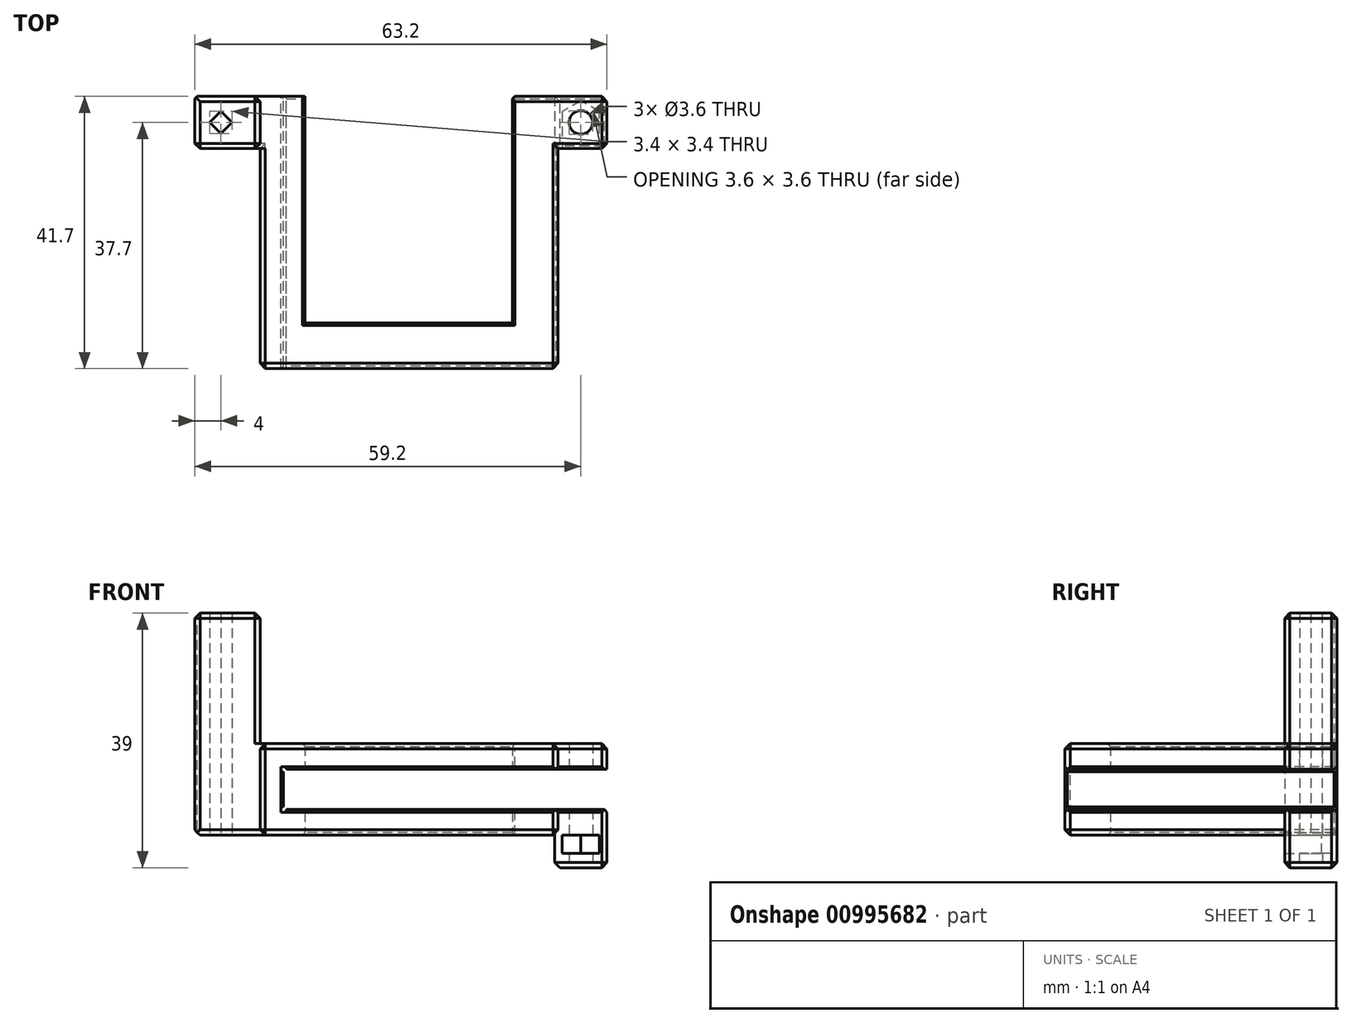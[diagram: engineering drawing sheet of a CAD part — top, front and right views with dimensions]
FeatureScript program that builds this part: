
annotation { "Feature Type Name" : "Feature", "Feature Type Description" : "" }
export const myFeature = defineFeature(function(context is Context, id is Id, definition is map)
    precondition{}
    {
        {
            var Q0;
            Q0=qCreatedBy(makeId("Top.planeOp"),FACE);
            var sketch = newSketch(context, id + "F0", { "sketchPlane" : qUnion([Q0])});
            skLineSegment(sketch, "E0.bottom", {"start": v(0, 0) * mm, "end": v(31.6, 0) * mm, "construction": true});
            skLineSegment(sketch, "E0.top", {"start": v(0, -31.6) * mm, "end": v(31.6, -31.6) * mm, "construction": true});
            skLineSegment(sketch, "E0.left", {"start": v(0, 0) * mm, "end": v(0, -31.6) * mm, "construction": true});
            skLineSegment(sketch, "E0.right", {"start": v(31.6, 0) * mm, "end": v(31.6, -31.6) * mm, "construction": true});
            skLineSegment(sketch, "E1.bottom", {"start": v(-3, 2) * mm, "end": v(57, 2) * mm, "construction": true});
            skLineSegment(sketch, "E1.top", {"start": v(-3, -48) * mm, "end": v(57, -48) * mm, "construction": true});
            skLineSegment(sketch, "E1.left", {"start": v(-3, 2) * mm, "end": v(-3, -48) * mm, "construction": true});
            skLineSegment(sketch, "E1.right", {"start": v(57, 2) * mm, "end": v(57, -48) * mm, "construction": true});
            skCircle(sketch, "E2", {"center": v(42.2, -1) * mm, "radius": 1.8 * mm});
            skLineSegment(sketch, "E3.bottom", {"start": v(-0.1, 2) * mm, "end": v(-7, 2) * mm});
            skLineSegment(sketch, "E3.top", {"start": v(-0.1, -38.7) * mm, "end": v(-7, -38.7) * mm});
            skLineSegment(sketch, "E3.left", {"start": v(-0.1, 2) * mm, "end": v(-0.1, -38.7) * mm});
            skLineSegment(sketch, "E3.right", {"start": v(-7, 2) * mm, "end": v(-7, -38.7) * mm});
            skLineSegment(sketch, "E4.bottom", {"start": v(-0.1, -38.7) * mm, "end": v(31.7, -38.7) * mm});
            skLineSegment(sketch, "E4.top", {"start": v(-0.1, -31.7) * mm, "end": v(31.7, -31.7) * mm});
            skLineSegment(sketch, "E4.left", {"start": v(-0.1, -38.7) * mm, "end": v(-0.1, -31.7) * mm});
            skLineSegment(sketch, "E4.right", {"start": v(31.7, -38.7) * mm, "end": v(31.7, -31.7) * mm});
            skLineSegment(sketch, "E5.bottom", {"start": v(31.7, -38.7) * mm, "end": v(38.7, -38.7) * mm});
            skLineSegment(sketch, "E5.top", {"start": v(31.7, 2) * mm, "end": v(38.7, 2) * mm});
            skLineSegment(sketch, "E5.left", {"start": v(31.7, -38.7) * mm, "end": v(31.7, 2) * mm});
            skLineSegment(sketch, "E5.right", {"start": v(38.7, -38.7) * mm, "end": v(38.7, 2) * mm});
            skLineSegment(sketch, "E6.bottom", {"start": v(38.7, 2) * mm, "end": v(46.2, 2) * mm});
            skLineSegment(sketch, "E6.top", {"start": v(38.7, -5) * mm, "end": v(46.2, -5) * mm});
            skLineSegment(sketch, "E6.left", {"start": v(38.7, 2) * mm, "end": v(38.7, -5) * mm});
            skLineSegment(sketch, "E6.right", {"start": v(46.2, 2) * mm, "end": v(46.2, -5) * mm});
            skCircle(sketch, "E7", {"center": v(42.2, -1) * mm, "radius": 4 * mm, "construction": true});
            skLineSegment(sketch, "E8.bottom", {"start": v(31.7, 2) * mm, "end": v(46.2, 2) * mm});
            skLineSegment(sketch, "E8.top", {"start": v(31.7, 3) * mm, "end": v(46.2, 3) * mm});
            skLineSegment(sketch, "E8.left", {"start": v(31.7, 2) * mm, "end": v(31.7, 3) * mm});
            skLineSegment(sketch, "E8.right", {"start": v(46.2, 2) * mm, "end": v(46.2, 3) * mm});
            skLineSegment(sketch, "E9.bottom", {"start": v(-7, 2) * mm, "end": v(-0.1, 2) * mm});
            skLineSegment(sketch, "E9.top", {"start": v(-7, 3) * mm, "end": v(-0.1, 3) * mm});
            skLineSegment(sketch, "E9.left", {"start": v(-7, 2) * mm, "end": v(-7, 3) * mm});
            skLineSegment(sketch, "E9.right", {"start": v(-0.1, 2) * mm, "end": v(-0.1, 3) * mm});
            skLineSegment(sketch, "E10", {"start": v(57, 2) * mm, "end": v(57, 8) * mm, "construction": true});
            skLineSegment(sketch, "E11.bottom", {"start": v(-7, 8) * mm, "end": v(57, 8) * mm, "construction": true});
            skLineSegment(sketch, "E11.top", {"start": v(-7, 5) * mm, "end": v(57, 5) * mm, "construction": true});
            skLineSegment(sketch, "E11.left", {"start": v(-7, 8) * mm, "end": v(-7, 5) * mm, "construction": true});
            skLineSegment(sketch, "E11.right", {"start": v(57, 8) * mm, "end": v(57, 5) * mm, "construction": true});
            skLineSegment(sketch, "E12", {"start": v(-7, 8) * mm, "end": v(-47, 8) * mm, "construction": true});
            skCircle(sketch, "E13", {"center": v(-13, -1) * mm, "radius": 4 * mm, "construction": true});
            skLineSegment(sketch, "E14.bottom", {"start": v(-0.1, 3) * mm, "end": v(-17, 3) * mm});
            skLineSegment(sketch, "E14.top", {"start": v(-0.1, -5) * mm, "end": v(-17, -5) * mm});
            skLineSegment(sketch, "E14.left", {"start": v(-0.1, 3) * mm, "end": v(-0.1, -5) * mm});
            skLineSegment(sketch, "E14.right", {"start": v(-17, 3) * mm, "end": v(-17, -5) * mm});
            skCircle(sketch, "E15", {"center": v(-13, -1) * mm, "radius": 1.7 * mm, "construction": true});
            skLineSegment(sketch, "E16.0", {"start": v(-11.3, -1) * mm, "end": v(-13, -2.7) * mm});
            skLineSegment(sketch, "E16.1", {"start": v(-13, -2.7) * mm, "end": v(-14.7, -1) * mm});
            skLineSegment(sketch, "E16.2", {"start": v(-14.7, -1) * mm, "end": v(-13, 0.7) * mm});
            skLineSegment(sketch, "E16.3", {"start": v(-13, 0.7) * mm, "end": v(-11.3, -1) * mm});
            skSolve(sketch);
        }
        {
            var Q0;
            {var subQ5=sQuery(id+"F0.wireOp",EDGE,"E9.left");Q0=makeQuery(id+"F0.imprint","IMPRINT",FACE,{"disambiguationData":[TD([[makeQuery(id+"F0.imprint","IMPRINT",EDGE,{"derivedFrom":subQ5}),1.0]])]});}
            extrude(context, id + "F1", {"entities" : qUnion([Q0]), "depth" : 27 * mm, "offsetDistance" : 25 * mm});
        }
        {
            var Q0;
            {var subQ5=sQuery(id+"F0.wireOp",EDGE,"E9.left");Q0=makeQuery(id+"F0.imprint","IMPRINT",FACE,{"disambiguationData":[TD([[makeQuery(id+"F0.imprint","IMPRINT",EDGE,{"derivedFrom":subQ5}),1.0]])]});}
            extrude(context, id + "F2", {"entities" : qUnion([Q0]), "operationType" : NewBodyOperationType.ADD, "oppositeDirection" : true, "depth" : 6 * mm, "offsetDistance" : 25 * mm});
        }
        {
            var Q0;
            Q0 = qSketchRegion(id + "F0", true);
            extrude(context, id + "F3", {"entities" : qUnion([Q0]), "operationType" : NewBodyOperationType.ADD, "endBound" : BoundingType.SYMMETRIC, "depth" : 14 * mm, "offsetDistance" : 25 * mm});
        }
        {
            var Q0;
            Q0=makeQuery(id+"F3.opExtrude","SWEPT_FACE",FACE,{"disambiguationData":[OSD([sQuery(id+"F0.wireOp",EDGE,"E8.top")])]});
            var sketch = newSketch(context, id + "F4", { "sketchPlane" : qUnion([Q0])});
            skLineSegment(sketch, "E17.bottom", {"start": v(-46.2, 3.1) * mm, "end": v(3.4, 3.1) * mm});
            skLineSegment(sketch, "E17.top", {"start": v(-46.2, -3.1) * mm, "end": v(3.4, -3.1) * mm});
            skLineSegment(sketch, "E17.left", {"start": v(-46.2, 3.1) * mm, "end": v(-46.2, -3.1) * mm});
            skLineSegment(sketch, "E17.right", {"start": v(3.4, 3.1) * mm, "end": v(3.4, -3.1) * mm});
            skPoint(sketch, "E17.middle", {"position": v(-21.4, 0) * mm});
            skPoint(sketch, "E18.0", {"position": v(3, 0) * mm});
            skLineSegment(sketch, "E19.bottom", {"start": v(3, 3.5) * mm, "end": v(3.8, 3.5) * mm});
            skLineSegment(sketch, "E19.top", {"start": v(3, 2.7) * mm, "end": v(3.8, 2.7) * mm});
            skLineSegment(sketch, "E19.left", {"start": v(3, 3.5) * mm, "end": v(3, 2.7) * mm});
            skLineSegment(sketch, "E19.right", {"start": v(3.8, 3.5) * mm, "end": v(3.8, 2.7) * mm});
            skPoint(sketch, "E19.middle", {"position": v(3.4, 3.1) * mm});
            skLineSegment(sketch, "E20.bottom", {"start": v(3, -2.7) * mm, "end": v(3.8, -2.7) * mm});
            skLineSegment(sketch, "E20.top", {"start": v(3, -3.5) * mm, "end": v(3.8, -3.5) * mm});
            skLineSegment(sketch, "E20.left", {"start": v(3, -2.7) * mm, "end": v(3, -3.5) * mm});
            skLineSegment(sketch, "E20.right", {"start": v(3.8, -2.7) * mm, "end": v(3.8, -3.5) * mm});
            skPoint(sketch, "E20.middle", {"position": v(3.4, -3.1) * mm});
            skSolve(sketch);
        }
        {
            var Q0;
            Q0 = qSketchRegion(id + "F4", true);
            var Q1;
            Q1=makeQuery(id+"F3.opExtrude","SWEPT_FACE",FACE,{"disambiguationData":[OSD([sQuery(id+"F0.wireOp",EDGE,"E3.top"),sQuery(id+"F0.wireOp",EDGE,"E4.bottom"),sQuery(id+"F0.wireOp",EDGE,"E5.bottom")])]});
            extrude(context, id + "F5", {"entities" : qUnion([Q0]), "operationType" : NewBodyOperationType.REMOVE, "endBound" : BoundingType.SYMMETRIC, "oppositeDirection" : true, "depth" : 100 * mm, "endBoundEntityFace" : qUnion([Q1]), "offsetDistance" : 25 * mm});
        }
        {
            var Q0;
            Q0=makeQuery(id+"F3.opExtrude","CAP_FACE",FACE,{"disambiguationData":[OSD([sQuery(id+"F0.wireOp",EDGE,"E2"),sQuery(id+"F0.wireOp",EDGE,"E3.top"),sQuery(id+"F0.wireOp",EDGE,"E3.left"),sQuery(id+"F0.wireOp",EDGE,"E3.right"),sQuery(id+"F0.wireOp",EDGE,"E4.bottom"),sQuery(id+"F0.wireOp",EDGE,"E4.top"),sQuery(id+"F0.wireOp",EDGE,"E5.bottom"),sQuery(id+"F0.wireOp",EDGE,"E5.left"),sQuery(id+"F0.wireOp",EDGE,"E5.right"),sQuery(id+"F0.wireOp",EDGE,"E6.top"),sQuery(id+"F0.wireOp",EDGE,"E6.right"),sQuery(id+"F0.wireOp",EDGE,"E8.top"),sQuery(id+"F0.wireOp",EDGE,"E8.left"),sQuery(id+"F0.wireOp",EDGE,"E8.right"),sQuery(id+"F0.wireOp",EDGE,"E14.bottom"),sQuery(id+"F0.wireOp",EDGE,"E14.top"),sQuery(id+"F0.wireOp",EDGE,"E14.left"),sQuery(id+"F0.wireOp",EDGE,"E14.right"),sQuery(id+"F0.wireOp",EDGE,"E16.0"),sQuery(id+"F0.wireOp",EDGE,"E16.1"),sQuery(id+"F0.wireOp",EDGE,"E16.2"),sQuery(id+"F0.wireOp",EDGE,"E16.3")])],"isStart":true});
            var sketch = newSketch(context, id + "F6", { "sketchPlane" : qUnion([Q0])});
            skLineSegment(sketch, "E21.bottom", {"start": v(46.2, -3) * mm, "end": v(38.2, -3) * mm});
            skLineSegment(sketch, "E21.top", {"start": v(46.2, 5) * mm, "end": v(38.2, 5) * mm});
            skLineSegment(sketch, "E21.left", {"start": v(46.2, -3) * mm, "end": v(46.2, 5) * mm});
            skLineSegment(sketch, "E21.right", {"start": v(38.2, -3) * mm, "end": v(38.2, 5) * mm});
            skCircle(sketch, "E22.0", {"center": v(42.2, 1) * mm, "radius": 1.8 * mm});
            skCircle(sketch, "E23", {"center": v(42.2, 1) * mm, "radius": 3.3 * mm, "construction": true});
            skLineSegment(sketch, "E24.0", {"start": v(42.2, 4.3) * mm, "end": v(45.06, 2.65) * mm});
            skLineSegment(sketch, "E24.1", {"start": v(45.06, 2.65) * mm, "end": v(45.06, -0.65) * mm});
            skLineSegment(sketch, "E24.2", {"start": v(45.06, -0.65) * mm, "end": v(42.2, -2.3) * mm});
            skLineSegment(sketch, "E24.3", {"start": v(42.2, -2.3) * mm, "end": v(39.34, -0.65) * mm});
            skLineSegment(sketch, "E24.4", {"start": v(39.34, -0.65) * mm, "end": v(39.34, 2.65) * mm});
            skLineSegment(sketch, "E24.5", {"start": v(39.34, 2.65) * mm, "end": v(42.2, 4.3) * mm});
            skLineSegment(sketch, "E25", {"start": v(39.34, 2.65) * mm, "end": v(39.34, 5) * mm});
            skLineSegment(sketch, "E26", {"start": v(45.06, 2.65) * mm, "end": v(45.06, 5) * mm});
            skSolve(sketch);
        }
        {
            var Q0;
            Q0 = qSketchRegion(id + "F6", true);
            var Q1;
            Q1=makeQuery(id+"F6.imprint","IMPRINT",FACE,{"disambiguationData":[TD([[makeQuery(id+"F6.imprint","IMPRINT",EDGE,{"derivedFrom":sQuery(id+"F6.wireOp",EDGE,"E22.0")}),1.0]])]});
            extrude(context, id + "F7", {"entities" : qUnion([Q0, Q1]), "operationType" : NewBodyOperationType.ADD, "flatOperationType" : FlatOperationType.REMOVE, "depth" : 5 * mm, "offsetDistance" : 25 * mm, "domain" : OperationDomain.MODEL});
        }
        {
            var Q0;
            Q0=makeQuery(id+"F6.imprint","IMPRINT",FACE,{"disambiguationData":[TD([[makeQuery(id+"F6.imprint","IMPRINT",EDGE,{"derivedFrom":sQuery(id+"F6.wireOp",EDGE,"E22.0")}),1.0]])]});
            var Q1;
            Q1=makeQuery(id+"F6.imprint","IMPRINT",FACE,{"disambiguationData":[TD([[makeQuery(id+"F6.imprint","IMPRINT",EDGE,{"derivedFrom":sQuery(id+"F6.wireOp",EDGE,"E24.0")}),1.0]])]});
            extrude(context, id + "F8", {"entities" : qUnion([Q0, Q1]), "operationType" : NewBodyOperationType.REMOVE, "depth" : 2.8 * mm, "offsetDistance" : 25 * mm});
        }
        {
            var Q0;
            {var subQ0=sQuery(id+"F0.wireOp",EDGE,"E14.bottom");Q0=makeQuery(id+"F5.boolean.opBoolean","INTERSECT",EDGE,{"derivedFrom":[makeQuery(id+"F3.boolean.opBoolean","MERGE",FACE,{"derivedFrom":[makeQuery(id+"F2.boolean.opBoolean","MERGE",FACE,{"derivedFrom":[makeQuery(id+"F1.opExtrude","SWEPT_FACE",FACE,{"disambiguationData":[OSD([subQ0])]}),makeQuery(id+"F2.opExtrude","SWEPT_FACE",FACE,{"disambiguationData":[OSD([subQ0])]})]}),makeQuery(id+"F3.opExtrude","SWEPT_FACE",FACE,{"disambiguationData":[OSD([subQ0])]})]}),makeQuery(id+"F5.opExtrude","SWEPT_FACE",FACE,{"disambiguationData":[OSD([sQuery(id+"F4.wireOp",EDGE,"E17.right")])]})]});}
            var Q1;
            Q1=makeQuery(id+"F5.boolean.opBoolean","INTERSECT",EDGE,{"derivedFrom":[makeQuery(id+"F3.opExtrude","SWEPT_FACE",FACE,{"disambiguationData":[OSD([sQuery(id+"F0.wireOp",EDGE,"E3.top"),sQuery(id+"F0.wireOp",EDGE,"E4.bottom"),sQuery(id+"F0.wireOp",EDGE,"E5.bottom")])]}),makeQuery(id+"F5.opExtrude","SWEPT_FACE",FACE,{"disambiguationData":[OSD([sQuery(id+"F4.wireOp",EDGE,"E17.right")])]})]});
            var Q2;
            {var subQ0=sQuery(id+"F0.wireOp",EDGE,"E14.bottom");Q2=makeQuery(id+"F5.boolean.opBoolean","INTERSECT",EDGE,{"derivedFrom":[makeQuery(id+"F3.boolean.opBoolean","MERGE",FACE,{"derivedFrom":[makeQuery(id+"F2.boolean.opBoolean","MERGE",FACE,{"derivedFrom":[makeQuery(id+"F1.opExtrude","SWEPT_FACE",FACE,{"disambiguationData":[OSD([subQ0])]}),makeQuery(id+"F2.opExtrude","SWEPT_FACE",FACE,{"disambiguationData":[OSD([subQ0])]})]}),makeQuery(id+"F3.opExtrude","SWEPT_FACE",FACE,{"disambiguationData":[OSD([subQ0])]})]}),makeQuery(id+"F5.opExtrude","SWEPT_FACE",FACE,{"disambiguationData":[OSD([sQuery(id+"F4.wireOp",EDGE,"E17.bottom")])]})]});}
            var Q3;
            {var subQ0=sQuery(id+"F0.wireOp",EDGE,"E14.bottom");Q3=makeQuery(id+"F5.boolean.opBoolean","INTERSECT",EDGE,{"derivedFrom":[makeQuery(id+"F3.boolean.opBoolean","MERGE",FACE,{"derivedFrom":[makeQuery(id+"F2.boolean.opBoolean","MERGE",FACE,{"derivedFrom":[makeQuery(id+"F1.opExtrude","SWEPT_FACE",FACE,{"disambiguationData":[OSD([subQ0])]}),makeQuery(id+"F2.opExtrude","SWEPT_FACE",FACE,{"disambiguationData":[OSD([subQ0])]})]}),makeQuery(id+"F3.opExtrude","SWEPT_FACE",FACE,{"disambiguationData":[OSD([subQ0])]})]}),makeQuery(id+"F5.opExtrude","SWEPT_FACE",FACE,{"disambiguationData":[OSD([sQuery(id+"F4.wireOp",EDGE,"E17.top")])]})]});}
            var Q4;
            Q4=makeQuery(id+"F5.boolean.opBoolean","INTERSECT",EDGE,{"derivedFrom":[makeQuery(id+"F3.opExtrude","SWEPT_FACE",FACE,{"disambiguationData":[OSD([sQuery(id+"F0.wireOp",EDGE,"E3.top"),sQuery(id+"F0.wireOp",EDGE,"E4.bottom"),sQuery(id+"F0.wireOp",EDGE,"E5.bottom")])]}),makeQuery(id+"F5.opExtrude","SWEPT_FACE",FACE,{"disambiguationData":[OSD([sQuery(id+"F4.wireOp",EDGE,"E17.bottom")])]})]});
            var Q5;
            Q5=makeQuery(id+"F5.boolean.opBoolean","INTERSECT",EDGE,{"derivedFrom":[makeQuery(id+"F3.opExtrude","SWEPT_FACE",FACE,{"disambiguationData":[OSD([sQuery(id+"F0.wireOp",EDGE,"E3.top"),sQuery(id+"F0.wireOp",EDGE,"E4.bottom"),sQuery(id+"F0.wireOp",EDGE,"E5.bottom")])]}),makeQuery(id+"F5.opExtrude","SWEPT_FACE",FACE,{"disambiguationData":[OSD([sQuery(id+"F4.wireOp",EDGE,"E17.top")])]})]});
            var Q6;
            Q6=makeQuery(id+"F5.boolean.opBoolean","INTERSECT",EDGE,{"derivedFrom":[makeQuery(id+"F3.opExtrude","SWEPT_FACE",FACE,{"disambiguationData":[OSD([sQuery(id+"F0.wireOp",EDGE,"E8.top")])]}),makeQuery(id+"F5.opExtrude","SWEPT_FACE",FACE,{"disambiguationData":[OSD([sQuery(id+"F4.wireOp",EDGE,"E17.bottom")])]})]});
            var Q7;
            Q7=makeQuery(id+"F5.boolean.opBoolean","INTERSECT",EDGE,{"derivedFrom":[makeQuery(id+"F3.opExtrude","SWEPT_FACE",FACE,{"disambiguationData":[OSD([sQuery(id+"F0.wireOp",EDGE,"E8.top")])]}),makeQuery(id+"F5.opExtrude","SWEPT_FACE",FACE,{"disambiguationData":[OSD([sQuery(id+"F4.wireOp",EDGE,"E17.top")])]})]});
            var Q8;
            Q8=makeQuery(id+"F5.boolean.opBoolean","INTERSECT",EDGE,{"derivedFrom":[makeQuery(id+"F3.opExtrude","SWEPT_FACE",FACE,{"disambiguationData":[OSD([sQuery(id+"F0.wireOp",EDGE,"E3.left"),sQuery(id+"F0.wireOp",EDGE,"E14.left")])]}),makeQuery(id+"F5.opExtrude","SWEPT_FACE",FACE,{"disambiguationData":[OSD([sQuery(id+"F4.wireOp",EDGE,"E17.top")])]})]});
            var Q9;
            Q9=makeQuery(id+"F5.boolean.opBoolean","INTERSECT",EDGE,{"derivedFrom":[makeQuery(id+"F3.opExtrude","SWEPT_FACE",FACE,{"disambiguationData":[OSD([sQuery(id+"F0.wireOp",EDGE,"E3.left"),sQuery(id+"F0.wireOp",EDGE,"E14.left")])]}),makeQuery(id+"F5.opExtrude","SWEPT_FACE",FACE,{"disambiguationData":[OSD([sQuery(id+"F4.wireOp",EDGE,"E17.bottom")])]})]});
            var Q10;
            Q10=makeQuery(id+"F5.boolean.opBoolean","INTERSECT",EDGE,{"derivedFrom":[makeQuery(id+"F3.opExtrude","SWEPT_FACE",FACE,{"disambiguationData":[OSD([sQuery(id+"F0.wireOp",EDGE,"E5.left"),sQuery(id+"F0.wireOp",EDGE,"E8.left")])]}),makeQuery(id+"F5.opExtrude","SWEPT_FACE",FACE,{"disambiguationData":[OSD([sQuery(id+"F4.wireOp",EDGE,"E17.bottom")])]})]});
            var Q11;
            Q11=makeQuery(id+"F5.boolean.opBoolean","INTERSECT",EDGE,{"derivedFrom":[makeQuery(id+"F3.opExtrude","SWEPT_FACE",FACE,{"disambiguationData":[OSD([sQuery(id+"F0.wireOp",EDGE,"E5.left"),sQuery(id+"F0.wireOp",EDGE,"E8.left")])]}),makeQuery(id+"F5.opExtrude","SWEPT_FACE",FACE,{"disambiguationData":[OSD([sQuery(id+"F4.wireOp",EDGE,"E17.top")])]})]});
            var Q12;
            Q12=makeQuery(id+"F5.boolean.opBoolean","INTERSECT",EDGE,{"derivedFrom":[makeQuery(id+"F3.opExtrude","SWEPT_FACE",FACE,{"disambiguationData":[OSD([sQuery(id+"F0.wireOp",EDGE,"E4.top")])]}),makeQuery(id+"F5.opExtrude","SWEPT_FACE",FACE,{"disambiguationData":[OSD([sQuery(id+"F4.wireOp",EDGE,"E17.top")])]})]});
            var Q13;
            Q13=makeQuery(id+"F5.boolean.opBoolean","INTERSECT",EDGE,{"derivedFrom":[makeQuery(id+"F3.opExtrude","SWEPT_FACE",FACE,{"disambiguationData":[OSD([sQuery(id+"F0.wireOp",EDGE,"E4.top")])]}),makeQuery(id+"F5.opExtrude","SWEPT_FACE",FACE,{"disambiguationData":[OSD([sQuery(id+"F4.wireOp",EDGE,"E17.bottom")])]})]});
            var Q14;
            Q14=makeQuery(id+"F5.boolean.opBoolean","INTERSECT",EDGE,{"derivedFrom":[makeQuery(id+"F3.opExtrude","SWEPT_FACE",FACE,{"disambiguationData":[OSD([sQuery(id+"F0.wireOp",EDGE,"E5.right")])]}),makeQuery(id+"F5.opExtrude","SWEPT_FACE",FACE,{"disambiguationData":[OSD([sQuery(id+"F4.wireOp",EDGE,"E17.bottom")])]})]});
            var Q15;
            Q15=makeQuery(id+"F5.boolean.opBoolean","INTERSECT",EDGE,{"derivedFrom":[makeQuery(id+"F3.opExtrude","SWEPT_FACE",FACE,{"disambiguationData":[OSD([sQuery(id+"F0.wireOp",EDGE,"E5.right")])]}),makeQuery(id+"F5.opExtrude","SWEPT_FACE",FACE,{"disambiguationData":[OSD([sQuery(id+"F4.wireOp",EDGE,"E17.top")])]})]});
            var Q16;
            Q16=makeQuery(id+"F5.boolean.opBoolean","INTERSECT",EDGE,{"derivedFrom":[makeQuery(id+"F3.opExtrude","SWEPT_FACE",FACE,{"disambiguationData":[OSD([sQuery(id+"F0.wireOp",EDGE,"E6.top")])]}),makeQuery(id+"F5.opExtrude","SWEPT_FACE",FACE,{"disambiguationData":[OSD([sQuery(id+"F4.wireOp",EDGE,"E17.top")])]})]});
            var Q17;
            Q17=makeQuery(id+"F5.boolean.opBoolean","COPY",EDGE,{"derivedFrom":makeQuery(id+"F5.opExtrude","SWEPT_EDGE",EDGE,{"disambiguationData":[OSD([sQuery(id+"F0.wireOp",EDGE,"E8.top"),sQuery(id+"F0.wireOp",EDGE,"E8.right"),sQuery(id+"F4.wireOp",EDGE,"E17.top"),sQuery(id+"F4.wireOp",EDGE,"E17.left")])]})});
            var Q18;
            Q18=makeQuery(id+"F5.boolean.opBoolean","INTERSECT",EDGE,{"derivedFrom":[makeQuery(id+"F3.opExtrude","SWEPT_FACE",FACE,{"disambiguationData":[OSD([sQuery(id+"F0.wireOp",EDGE,"E6.top")])]}),makeQuery(id+"F5.opExtrude","SWEPT_FACE",FACE,{"disambiguationData":[OSD([sQuery(id+"F4.wireOp",EDGE,"E17.bottom")])]})]});
            var Q19;
            Q19=makeQuery(id+"F5.boolean.opBoolean","COPY",EDGE,{"derivedFrom":makeQuery(id+"F5.opExtrude","SWEPT_EDGE",EDGE,{"disambiguationData":[OSD([sQuery(id+"F0.wireOp",EDGE,"E8.top"),sQuery(id+"F0.wireOp",EDGE,"E8.right"),sQuery(id+"F4.wireOp",EDGE,"E17.bottom"),sQuery(id+"F4.wireOp",EDGE,"E17.left")])]})});
            var Q20;
            Q20=makeQuery(id+"F3.opExtrude","CAP_EDGE",EDGE,{"disambiguationData":[OSD([sQuery(id+"F0.wireOp",EDGE,"E5.left"),sQuery(id+"F0.wireOp",EDGE,"E8.left")])],"isStart":false});
            var Q21;
            Q21=makeQuery(id+"F3.opExtrude","CAP_EDGE",EDGE,{"disambiguationData":[OSD([sQuery(id+"F0.wireOp",EDGE,"E4.top")])],"isStart":false});
            var Q22;
            Q22=makeQuery(id+"F3.opExtrude","CAP_EDGE",EDGE,{"disambiguationData":[OSD([sQuery(id+"F0.wireOp",EDGE,"E3.left"),sQuery(id+"F0.wireOp",EDGE,"E14.left")])],"isStart":false});
            var Q23;
            Q23=makeQuery(id+"F3.opExtrude","CAP_EDGE",EDGE,{"disambiguationData":[OSD([sQuery(id+"F0.wireOp",EDGE,"E4.top")])],"isStart":true});
            var Q24;
            Q24=makeQuery(id+"F3.opExtrude","CAP_EDGE",EDGE,{"disambiguationData":[OSD([sQuery(id+"F0.wireOp",EDGE,"E5.left"),sQuery(id+"F0.wireOp",EDGE,"E8.left")])],"isStart":true});
            var Q25;
            Q25=makeQuery(id+"F3.opExtrude","CAP_EDGE",EDGE,{"disambiguationData":[OSD([sQuery(id+"F0.wireOp",EDGE,"E3.left"),sQuery(id+"F0.wireOp",EDGE,"E14.left")])],"isStart":true});
            var Q26;
            {var subQ0=sQuery(id+"F0.wireOp",EDGE,"E8.left");var subQ1=sQuery(id+"F0.wireOp",EDGE,"E8.top");Q26=makeQuery(id+"F5.boolean.opBoolean","SPLIT",EDGE,{"disambiguationData":[TD([makeQuery(id+"F5.opExtrude","SWEPT_FACE",FACE,{"disambiguationData":[OSD([sQuery(id+"F4.wireOp",EDGE,"E17.bottom")])]})])],"derivedFrom":makeQuery(id+"F3.opExtrude","SWEPT_EDGE",EDGE,{"disambiguationData":[OSD([subQ1,subQ0])]})});}
            var Q27;
            {var subQ0=sQuery(id+"F0.wireOp",EDGE,"E8.left");var subQ1=sQuery(id+"F0.wireOp",EDGE,"E8.top");Q27=makeQuery(id+"F5.boolean.opBoolean","SPLIT",EDGE,{"disambiguationData":[TD([makeQuery(id+"F5.opExtrude","SWEPT_FACE",FACE,{"disambiguationData":[OSD([sQuery(id+"F4.wireOp",EDGE,"E17.top")])]})])],"derivedFrom":makeQuery(id+"F3.opExtrude","SWEPT_EDGE",EDGE,{"disambiguationData":[OSD([subQ1,subQ0])]})});}
            var Q28;
            {var subQ0=sQuery(id+"F0.wireOp",EDGE,"E14.left");var subQ2=sQuery(id+"F0.wireOp",EDGE,"E14.bottom");Q28=makeQuery(id+"F5.boolean.opBoolean","SPLIT",EDGE,{"disambiguationData":[TD([makeQuery(id+"F5.opExtrude","SWEPT_FACE",FACE,{"disambiguationData":[OSD([sQuery(id+"F4.wireOp",EDGE,"E17.bottom")])]})])],"derivedFrom":makeQuery(id+"F3.opExtrude","SWEPT_EDGE",EDGE,{"disambiguationData":[OSD([subQ2,subQ0])]})});}
            var Q29;
            {var subQ0=sQuery(id+"F0.wireOp",EDGE,"E14.left");var subQ2=sQuery(id+"F0.wireOp",EDGE,"E14.bottom");Q29=makeQuery(id+"F5.boolean.opBoolean","SPLIT",EDGE,{"disambiguationData":[TD([makeQuery(id+"F5.opExtrude","SWEPT_FACE",FACE,{"disambiguationData":[OSD([sQuery(id+"F4.wireOp",EDGE,"E17.top")])]})])],"derivedFrom":makeQuery(id+"F3.opExtrude","SWEPT_EDGE",EDGE,{"disambiguationData":[OSD([subQ2,subQ0])]})});}
            chamfer(context, id + "F9", {"entities" : qUnion([Q0, Q1, Q2, Q3, Q4, Q5, Q6, Q7, Q8, Q9, Q10, Q11, Q12, Q13, Q14, Q15, Q16, Q17, Q18, Q19, Q20, Q21, Q22, Q23, Q24, Q25, Q26, Q27, Q28, Q29]), "width" : 0.4 * mm});
        }
        {
            var Q0;
            {var subQ0=sQuery(id+"F0.wireOp",EDGE,"E14.right");var subQ1=sQuery(id+"F0.wireOp",EDGE,"E14.top");Q0=makeQuery(id+"F3.boolean.opBoolean","MERGE",EDGE,{"derivedFrom":[makeQuery(id+"F2.boolean.opBoolean","MERGE",EDGE,{"derivedFrom":[makeQuery(id+"F1.opExtrude","SWEPT_EDGE",EDGE,{"disambiguationData":[OSD([subQ1,subQ0])]}),makeQuery(id+"F2.opExtrude","SWEPT_EDGE",EDGE,{"disambiguationData":[OSD([subQ1,subQ0])]})]}),makeQuery(id+"F3.opExtrude","SWEPT_EDGE",EDGE,{"disambiguationData":[OSD([subQ1,subQ0])]})]});}
            var Q1;
            {var subQ0=sQuery(id+"F0.wireOp",EDGE,"E14.top");var subQ1=sQuery(id+"F0.wireOp",EDGE,"E3.right");Q1=makeQuery(id+"F3.boolean.opBoolean","SPLIT",EDGE,{"derivedFrom":makeQuery(id+"F2.boolean.opBoolean","MERGE",EDGE,{"derivedFrom":[makeQuery(id+"F1.opExtrude","SWEPT_EDGE",EDGE,{"disambiguationData":[OSD([subQ1,subQ0])]}),makeQuery(id+"F2.opExtrude","SWEPT_EDGE",EDGE,{"disambiguationData":[OSD([subQ1,subQ0])]})]})});}
            var Q2;
            {var subQ0=sQuery(id+"F0.wireOp",EDGE,"E14.bottom");var subQ1=sQuery(id+"F0.wireOp",EDGE,"E9.left");Q2=makeQuery(id+"F2.boolean.opBoolean","MERGE",EDGE,{"derivedFrom":[makeQuery(id+"F1.opExtrude","SWEPT_EDGE",EDGE,{"disambiguationData":[OSD([subQ1,subQ0])]}),makeQuery(id+"F2.opExtrude","SWEPT_EDGE",EDGE,{"disambiguationData":[OSD([subQ1,subQ0])]})]});}
            var Q3;
            {var subQ0=sQuery(id+"F0.wireOp",EDGE,"E14.right");var subQ1=sQuery(id+"F0.wireOp",EDGE,"E14.bottom");Q3=makeQuery(id+"F3.boolean.opBoolean","MERGE",EDGE,{"derivedFrom":[makeQuery(id+"F2.boolean.opBoolean","MERGE",EDGE,{"derivedFrom":[makeQuery(id+"F1.opExtrude","SWEPT_EDGE",EDGE,{"disambiguationData":[OSD([subQ1,subQ0])]}),makeQuery(id+"F2.opExtrude","SWEPT_EDGE",EDGE,{"disambiguationData":[OSD([subQ1,subQ0])]})]}),makeQuery(id+"F3.opExtrude","SWEPT_EDGE",EDGE,{"disambiguationData":[OSD([subQ1,subQ0])]})]});}
            var Q4;
            Q4=makeQuery(id+"F1.opExtrude","CAP_EDGE",EDGE,{"disambiguationData":[OSD([sQuery(id+"F0.wireOp",EDGE,"E14.bottom")])],"isStart":false});
            var Q5;
            Q5=makeQuery(id+"F1.opExtrude","CAP_EDGE",EDGE,{"disambiguationData":[OSD([sQuery(id+"F0.wireOp",EDGE,"E14.right")])],"isStart":false});
            var Q6;
            Q6=makeQuery(id+"F1.opExtrude","CAP_EDGE",EDGE,{"disambiguationData":[OSD([sQuery(id+"F0.wireOp",EDGE,"E3.right"),sQuery(id+"F0.wireOp",EDGE,"E9.left")])],"isStart":false});
            var Q7;
            Q7=makeQuery(id+"F1.opExtrude","CAP_EDGE",EDGE,{"disambiguationData":[OSD([sQuery(id+"F0.wireOp",EDGE,"E14.top")])],"isStart":false});
            var Q8;
            Q8=makeQuery(id+"F3.opExtrude","CAP_EDGE",EDGE,{"disambiguationData":[OSD([sQuery(id+"F0.wireOp",EDGE,"E14.right")])],"isStart":true});
            chamfer(context, id + "F10", {"entities" : qUnion([Q0, Q1, Q2, Q3, Q4, Q5, Q6, Q7, Q8]), "width" : 0.8 * mm, "tangentPropagation" : true});
        }
        {
            var Q0;
            Q0=makeQuery(id+"F3.opExtrude","CAP_EDGE",EDGE,{"disambiguationData":[OSD([sQuery(id+"F0.wireOp",EDGE,"E14.top")])],"isStart":true});
            var Q1;
            Q1=makeQuery(id+"F3.opExtrude","CAP_EDGE",EDGE,{"disambiguationData":[OSD([sQuery(id+"F0.wireOp",EDGE,"E3.right")])],"isStart":true});
            var Q2;
            Q2=makeQuery(id+"F3.opExtrude","CAP_EDGE",EDGE,{"disambiguationData":[OSD([sQuery(id+"F0.wireOp",EDGE,"E3.top"),sQuery(id+"F0.wireOp",EDGE,"E4.bottom"),sQuery(id+"F0.wireOp",EDGE,"E5.bottom")])],"isStart":true});
            var Q3;
            Q3=makeQuery(id+"F3.opExtrude","CAP_EDGE",EDGE,{"disambiguationData":[OSD([sQuery(id+"F0.wireOp",EDGE,"E3.right")])],"isStart":false});
            var Q4;
            Q4=makeQuery(id+"F3.opExtrude","CAP_EDGE",EDGE,{"disambiguationData":[OSD([sQuery(id+"F0.wireOp",EDGE,"E3.top"),sQuery(id+"F0.wireOp",EDGE,"E4.bottom"),sQuery(id+"F0.wireOp",EDGE,"E5.bottom")])],"isStart":false});
            var Q5;
            Q5=makeQuery(id+"F3.opExtrude","CAP_EDGE",EDGE,{"disambiguationData":[OSD([sQuery(id+"F0.wireOp",EDGE,"E5.right")])],"isStart":false});
            var Q6;
            Q6=makeQuery(id+"F3.opExtrude","CAP_EDGE",EDGE,{"disambiguationData":[OSD([sQuery(id+"F0.wireOp",EDGE,"E6.top")])],"isStart":false});
            var Q7;
            Q7=makeQuery(id+"F3.opExtrude","CAP_EDGE",EDGE,{"disambiguationData":[OSD([sQuery(id+"F0.wireOp",EDGE,"E6.right"),sQuery(id+"F0.wireOp",EDGE,"E8.right")])],"isStart":false});
            var Q8;
            Q8=makeQuery(id+"F3.opExtrude","CAP_EDGE",EDGE,{"disambiguationData":[OSD([sQuery(id+"F0.wireOp",EDGE,"E8.top")])],"isStart":false});
            var Q9;
            Q9=makeQuery(id+"F7.opExtrude","CAP_EDGE",EDGE,{"disambiguationData":[OSD([sQuery(id+"F6.wireOp",EDGE,"E21.left")])],"isStart":false});
            var Q10;
            {var subQ1=sQuery(id+"F0.wireOp",EDGE,"E6.right");var subQ2=sQuery(id+"F0.wireOp",EDGE,"E6.top");Q10=makeQuery(id+"F7.boolean.opBoolean","MERGE",EDGE,{"derivedFrom":[makeQuery(id+"F5.boolean.opBoolean","SPLIT",EDGE,{"disambiguationData":[TD([makeQuery(id+"F5.opExtrude","SWEPT_FACE",FACE,{"disambiguationData":[OSD([sQuery(id+"F4.wireOp",EDGE,"E17.top")])]})])],"derivedFrom":makeQuery(id+"F3.opExtrude","SWEPT_EDGE",EDGE,{"disambiguationData":[OSD([subQ2,subQ1])]})}),makeQuery(id+"F7.opExtrude","SWEPT_EDGE",EDGE,{"disambiguationData":[OSD([sQuery(id+"F6.wireOp",EDGE,"E21.top"),sQuery(id+"F6.wireOp",EDGE,"E21.left")])]})]});}
            var Q11;
            Q11=makeQuery(id+"F7.opExtrude","CAP_EDGE",EDGE,{"disambiguationData":[OSD([sQuery(id+"F6.wireOp",EDGE,"E21.bottom")])],"isStart":false});
            var Q12;
            Q12=makeQuery(id+"F7.opExtrude","CAP_EDGE",EDGE,{"disambiguationData":[OSD([sQuery(id+"F6.wireOp",EDGE,"E21.right")])],"isStart":false});
            var Q13;
            Q13=makeQuery(id+"F7.opExtrude","CAP_EDGE",EDGE,{"disambiguationData":[OSD([sQuery(id+"F6.wireOp",EDGE,"E21.top")])],"isStart":false});
            var Q14;
            Q14=makeQuery(id+"F3.opExtrude","CAP_EDGE",EDGE,{"disambiguationData":[OSD([sQuery(id+"F0.wireOp",EDGE,"E14.bottom")])],"isStart":true});
            var Q15;
            Q15=makeQuery(id+"F3.opExtrude","SWEPT_EDGE",EDGE,{"disambiguationData":[OSD([sQuery(id+"F0.wireOp",EDGE,"E3.top"),sQuery(id+"F0.wireOp",EDGE,"E3.right")])]});
            var Q16;
            {var subQ0=sQuery(id+"F0.wireOp",EDGE,"E5.right");var subQ1=sQuery(id+"F0.wireOp",EDGE,"E5.bottom");Q16=makeQuery(id+"F5.boolean.opBoolean","SPLIT",EDGE,{"disambiguationData":[TD([makeQuery(id+"F5.opExtrude","SWEPT_FACE",FACE,{"disambiguationData":[OSD([sQuery(id+"F4.wireOp",EDGE,"E17.top")])]})])],"derivedFrom":makeQuery(id+"F3.opExtrude","SWEPT_EDGE",EDGE,{"disambiguationData":[OSD([subQ1,subQ0])]})});}
            var Q17;
            {var subQ0=sQuery(id+"F0.wireOp",EDGE,"E5.right");var subQ1=sQuery(id+"F0.wireOp",EDGE,"E5.bottom");Q17=makeQuery(id+"F5.boolean.opBoolean","SPLIT",EDGE,{"disambiguationData":[TD([makeQuery(id+"F5.opExtrude","SWEPT_FACE",FACE,{"disambiguationData":[OSD([sQuery(id+"F4.wireOp",EDGE,"E17.bottom")])]})])],"derivedFrom":makeQuery(id+"F3.opExtrude","SWEPT_EDGE",EDGE,{"disambiguationData":[OSD([subQ1,subQ0])]})});}
            var Q18;
            {var subQ1=sQuery(id+"F0.wireOp",EDGE,"E6.right");var subQ2=sQuery(id+"F0.wireOp",EDGE,"E6.top");Q18=makeQuery(id+"F5.boolean.opBoolean","SPLIT",EDGE,{"disambiguationData":[TD([makeQuery(id+"F5.opExtrude","SWEPT_FACE",FACE,{"disambiguationData":[OSD([sQuery(id+"F4.wireOp",EDGE,"E17.bottom")])]})])],"derivedFrom":makeQuery(id+"F3.opExtrude","SWEPT_EDGE",EDGE,{"disambiguationData":[OSD([subQ2,subQ1])]})});}
            var Q19;
            {var subQ0=sQuery(id+"F0.wireOp",EDGE,"E8.right");var subQ1=sQuery(id+"F0.wireOp",EDGE,"E8.top");Q19=makeQuery(id+"F5.boolean.opBoolean","SPLIT",EDGE,{"disambiguationData":[TD([makeQuery(id+"F5.opExtrude","SWEPT_FACE",FACE,{"disambiguationData":[OSD([sQuery(id+"F4.wireOp",EDGE,"E17.bottom")])]})])],"derivedFrom":makeQuery(id+"F3.opExtrude","SWEPT_EDGE",EDGE,{"disambiguationData":[OSD([subQ1,subQ0])]})});}
            var Q20;
            {var subQ0=sQuery(id+"F0.wireOp",EDGE,"E8.right");var subQ1=sQuery(id+"F0.wireOp",EDGE,"E8.top");Q20=makeQuery(id+"F7.boolean.opBoolean","MERGE",EDGE,{"derivedFrom":[makeQuery(id+"F5.boolean.opBoolean","SPLIT",EDGE,{"disambiguationData":[TD([makeQuery(id+"F5.opExtrude","SWEPT_FACE",FACE,{"disambiguationData":[OSD([sQuery(id+"F4.wireOp",EDGE,"E17.top")])]})])],"derivedFrom":makeQuery(id+"F3.opExtrude","SWEPT_EDGE",EDGE,{"disambiguationData":[OSD([subQ1,subQ0])]})}),makeQuery(id+"F7.opExtrude","SWEPT_EDGE",EDGE,{"disambiguationData":[OSD([sQuery(id+"F6.wireOp",EDGE,"E21.bottom"),sQuery(id+"F6.wireOp",EDGE,"E21.left")])]})]});}
            var Q21;
            Q21=makeQuery(id+"F3.opExtrude","CAP_EDGE",EDGE,{"disambiguationData":[OSD([sQuery(id+"F0.wireOp",EDGE,"E5.right")])],"isStart":true});
            chamfer(context, id + "F11", {"entities" : qUnion([Q0, Q1, Q2, Q3, Q4, Q5, Q6, Q7, Q8, Q9, Q10, Q11, Q12, Q13, Q14, Q15, Q16, Q17, Q18, Q19, Q20, Q21]), "width" : 0.8 * mm, "tangentPropagation" : true});
        }
    });
